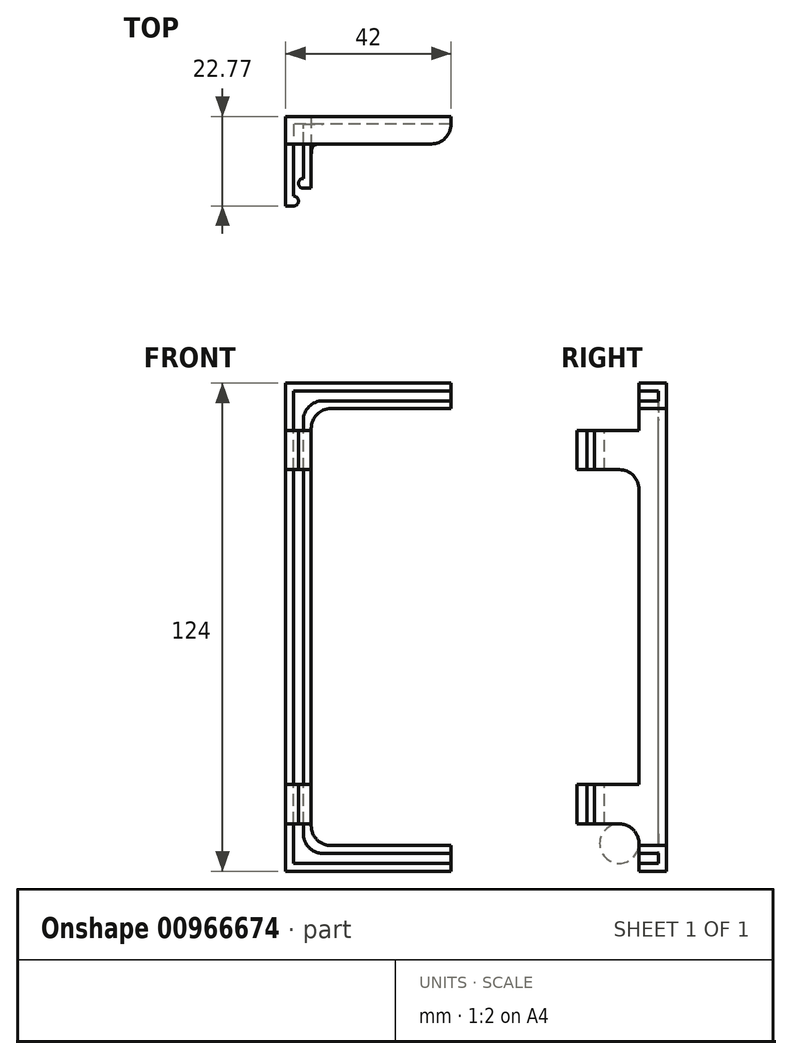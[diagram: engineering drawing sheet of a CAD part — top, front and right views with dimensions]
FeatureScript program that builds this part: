
annotation { "Feature Type Name" : "Feature", "Feature Type Description" : "" }
export const myFeature = defineFeature(function(context is Context, id is Id, definition is map)
    precondition{}
    {
        {
            var Q0;
            Q0=qCreatedBy(makeId("Top.planeOp"),FACE);
            var sketch = newSketch(context, id + "F0", { "sketchPlane" : qUnion([Q0])});
            skArc(sketch, "E0", {"start": v(0, -2.5) * mm, "mid": v(1.25, -1.25) * mm, "end": v(0, 0) * mm});
            skLineSegment(sketch, "E1", {"start": v(0, -1.25) * mm, "end": v(0, 11.7) * mm, "construction": true});
            skLineSegment(sketch, "E2", {"start": v(0, 2) * mm, "end": v(2.5, 2) * mm, "construction": true});
            skLineSegment(sketch, "E3", {"start": v(2.5, 2) * mm, "end": v(2.5, 8.7) * mm, "construction": true});
            skArc(sketch, "E4", {"start": v(2.5, 4.5) * mm, "mid": v(1.25, 3.25) * mm, "end": v(2.5, 2) * mm});
            skLineSegment(sketch, "E5", {"start": v(0, -2.5) * mm, "end": v(-2, -2.5) * mm});
            skLineSegment(sketch, "E6", {"start": v(-2, -2.5) * mm, "end": v(-2, 20.27) * mm});
            skLineSegment(sketch, "E7", {"start": v(2.5, 2) * mm, "end": v(4.5, 2) * mm});
            skLineSegment(sketch, "E8", {"start": v(4.5, 2) * mm, "end": v(4.5, 20.27) * mm});
            skLineSegment(sketch, "E9", {"start": v(4.5, 20.27) * mm, "end": v(-2, 20.27) * mm});
            skLineSegment(sketch, "E10", {"start": v(2.5, 4.5) * mm, "end": v(2.5, 18.27) * mm});
            skLineSegment(sketch, "E11", {"start": v(0, 0) * mm, "end": v(0, 18.27) * mm});
            skLineSegment(sketch, "E12", {"start": v(0, 18.27) * mm, "end": v(2.5, 18.27) * mm});
            skLineSegment(sketch, "E13", {"start": v(4.5, 13.27) * mm, "end": v(-2, 13.27) * mm});
            skSolve(sketch);
        }
        {
            var Q0;
            Q0=qCreatedBy(makeId("Front.planeOp"),FACE);
            var sketch = newSketch(context, id + "F1", { "sketchPlane" : qUnion([Q0])});
            skLineSegment(sketch, "E14", {"start": v(0, 0) * mm, "end": v(0, 120) * mm});
            skLineSegment(sketch, "E15", {"start": v(0, 120) * mm, "end": v(40, 120) * mm});
            skLineSegment(sketch, "E16", {"start": v(0, 0) * mm, "end": v(40, 0) * mm});
            skSolve(sketch);
        }
        {
            var Q0;
            {var subQ4=sQuery(id+"F0.wireOp",EDGE,"E9");Q0=makeQuery(id+"F0.imprint","IMPRINT",FACE,{"disambiguationData":[TD([[makeQuery(id+"F0.imprint","IMPRINT",EDGE,{"derivedFrom":subQ4}),1.0]])]});}
            var Q1;
            Q1=sQuery(id+"F1.wireOp",EDGE,"E14");
            var Q2;
            Q2=sQuery(id+"F1.wireOp",EDGE,"E15");
            var Q3;
            Q3=sQuery(id+"F1.wireOp",EDGE,"E16");
            sweep(context, id + "F2", {"profiles" : qUnion([Q0]), "path" : qUnion([Q1, Q2, Q3])});
        }
        {
            var Q0;
            Q0=qCreatedBy(makeId("Front.planeOp"),FACE);
            var sketch = newSketch(context, id + "F3", { "sketchPlane" : qUnion([Q0])});
            skLineSegment(sketch, "E17", {"start": v(0, 10) * mm, "end": v(0, 20) * mm});
            skLineSegment(sketch, "E18", {"start": v(0, 110) * mm, "end": v(0, 100) * mm});
            skSolve(sketch);
        }
        {
            var Q0;
            {var subQ1=sQuery(id+"F0.wireOp",EDGE,"E0");Q0=makeQuery(id+"F0.imprint","IMPRINT",FACE,{"disambiguationData":[TD([[makeQuery(id+"F0.imprint","IMPRINT",EDGE,{"derivedFrom":subQ1}),1.0]])]});}
            var Q1;
            Q1=sQuery(id+"F3.wireOp",VERTEX,"E17.start");
            cPlane(context, id + "F4", {"entities" : qUnion([Q0, Q1]), "cplaneType" : CPlaneType.PLANE_POINT, "offset" : 25 * mm, "width" : 150 * mm, "height" : 150 * mm});
        }
        {
            var Q0;
            {var subQ1=sQuery(id+"F0.wireOp",EDGE,"E0");Q0=makeQuery(id+"F0.imprint","IMPRINT",FACE,{"disambiguationData":[TD([[makeQuery(id+"F0.imprint","IMPRINT",EDGE,{"derivedFrom":subQ1}),1.0]])]});}
            var Q1;
            Q1=sQuery(id+"F3.wireOp",VERTEX,"E18.end");
            cPlane(context, id + "F5", {"entities" : qUnion([Q0, Q1]), "cplaneType" : CPlaneType.PLANE_POINT, "offset" : 25 * mm, "width" : 150 * mm, "height" : 150 * mm});
        }
        {
            var Q0;
            Q0=qCreatedBy(id+"F4.planeOp",FACE);
            var sketch = newSketch(context, id + "F6", { "sketchPlane" : qUnion([Q0])});
            skLineSegment(sketch, "E19.0.0", {"start": v(0, 0) * mm, "end": v(0, 13.27) * mm});
            skLineSegment(sketch, "E19.0.1", {"start": v(0, 13.27) * mm, "end": v(-2, 13.27) * mm});
            skLineSegment(sketch, "E19.0.2", {"start": v(-2, 13.27) * mm, "end": v(-2, -2.5) * mm});
            skLineSegment(sketch, "E19.0.3", {"start": v(-2, -2.5) * mm, "end": v(0, -2.5) * mm});
            skArc(sketch, "E19.0.4", {"start": v(0, -2.5) * mm, "mid": v(1.25, -1.25) * mm, "end": v(0, 0) * mm});
            skLineSegment(sketch, "E20.0.0", {"start": v(2.5, 13.27) * mm, "end": v(2.5, 4.5) * mm});
            skArc(sketch, "E20.0.1", {"start": v(2.5, 4.5) * mm, "mid": v(1.25, 3.25) * mm, "end": v(2.5, 2) * mm});
            skLineSegment(sketch, "E20.0.2", {"start": v(2.5, 2) * mm, "end": v(4.5, 2) * mm});
            skLineSegment(sketch, "E20.0.3", {"start": v(4.5, 2) * mm, "end": v(4.5, 13.27) * mm});
            skLineSegment(sketch, "E20.0.4", {"start": v(4.5, 13.27) * mm, "end": v(2.5, 13.27) * mm});
            skSolve(sketch);
        }
        {
            var Q0;
            Q0=qCreatedBy(id+"F5.planeOp",FACE);
            var sketch = newSketch(context, id + "F7", { "sketchPlane" : qUnion([Q0])});
            skLineSegment(sketch, "E21.0.0", {"start": v(0, 0) * mm, "end": v(0, 13.27) * mm});
            skLineSegment(sketch, "E21.0.1", {"start": v(0, 13.27) * mm, "end": v(-2, 13.27) * mm});
            skLineSegment(sketch, "E21.0.2", {"start": v(-2, 13.27) * mm, "end": v(-2, -2.5) * mm});
            skLineSegment(sketch, "E21.0.3", {"start": v(-2, -2.5) * mm, "end": v(0, -2.5) * mm});
            skArc(sketch, "E21.0.4", {"start": v(0, -2.5) * mm, "mid": v(1.25, -1.25) * mm, "end": v(0, 0) * mm});
            skLineSegment(sketch, "E22.0.0", {"start": v(2.5, 13.27) * mm, "end": v(2.5, 4.5) * mm});
            skArc(sketch, "E22.0.1", {"start": v(2.5, 4.5) * mm, "mid": v(1.25, 3.25) * mm, "end": v(2.5, 2) * mm});
            skLineSegment(sketch, "E22.0.2", {"start": v(2.5, 2) * mm, "end": v(4.5, 2) * mm});
            skLineSegment(sketch, "E22.0.3", {"start": v(4.5, 2) * mm, "end": v(4.5, 13.27) * mm});
            skLineSegment(sketch, "E22.0.4", {"start": v(4.5, 13.27) * mm, "end": v(2.5, 13.27) * mm});
            skSolve(sketch);
        }
        {
            var Q0;
            Q0=makeQuery(id+"F6.imprint","IMPRINT",FACE,{"disambiguationData":[TD([[makeQuery(id+"F6.imprint","IMPRINT",EDGE,{"derivedFrom":sQuery(id+"F6.wireOp",EDGE,"E19.0.0")}),1.0]])]});
            var Q1;
            Q1=makeQuery(id+"F6.imprint","IMPRINT",FACE,{"disambiguationData":[TD([[makeQuery(id+"F6.imprint","IMPRINT",EDGE,{"derivedFrom":sQuery(id+"F6.wireOp",EDGE,"E20.0.0")}),1.0]])]});
            var Q2;
            Q2=sQuery(id+"F3.wireOp",EDGE,"E17");
            sweep(context, id + "F8", {"operationType" : NewBodyOperationType.ADD, "profiles" : qUnion([Q0, Q1]), "path" : qUnion([Q2])});
        }
        {
            var Q0;
            Q0=makeQuery(id+"F7.imprint","IMPRINT",FACE,{"disambiguationData":[TD([[makeQuery(id+"F7.imprint","IMPRINT",EDGE,{"derivedFrom":sQuery(id+"F7.wireOp",EDGE,"E21.0.0")}),1.0]])]});
            var Q1;
            Q1=makeQuery(id+"F7.imprint","IMPRINT",FACE,{"disambiguationData":[TD([[makeQuery(id+"F7.imprint","IMPRINT",EDGE,{"derivedFrom":sQuery(id+"F7.wireOp",EDGE,"E22.0.0")}),1.0]])]});
            var Q2;
            Q2=sQuery(id+"F3.wireOp",EDGE,"E18");
            sweep(context, id + "F9", {"operationType" : NewBodyOperationType.ADD, "profiles" : qUnion([Q0, Q1]), "path" : qUnion([Q2])});
        }
        {
            var Q0;
            Q0=makeQuery(id+"F8.opSweep","CAP_EDGE",EDGE,{"disambiguationData":[OSD([sQuery(id+"F3.wireOp",VERTEX,"E17.start"),sQuery(id+"F6.wireOp",EDGE,"E19.0.1")])],"isStart":true});
            var Q1;
            Q1=makeQuery(id+"F8.opSweep","CAP_EDGE",EDGE,{"disambiguationData":[OSD([sQuery(id+"F3.wireOp",VERTEX,"E17.start"),sQuery(id+"F6.wireOp",EDGE,"E20.0.4")])],"isStart":true});
            var Q2;
            Q2=makeQuery(id+"F8.opSweep","CAP_EDGE",EDGE,{"disambiguationData":[OSD([sQuery(id+"F3.wireOp",VERTEX,"E17.end"),sQuery(id+"F6.wireOp",EDGE,"E19.0.1")])],"isStart":false});
            var Q3;
            Q3=makeQuery(id+"F8.opSweep","CAP_EDGE",EDGE,{"disambiguationData":[OSD([sQuery(id+"F3.wireOp",VERTEX,"E17.end"),sQuery(id+"F6.wireOp",EDGE,"E20.0.4")])],"isStart":false});
            var Q4;
            Q4=makeQuery(id+"F9.opSweep","CAP_EDGE",EDGE,{"disambiguationData":[OSD([sQuery(id+"F3.wireOp",VERTEX,"E18.end"),sQuery(id+"F7.wireOp",EDGE,"E21.0.1")])],"isStart":true});
            var Q5;
            Q5=makeQuery(id+"F9.opSweep","CAP_EDGE",EDGE,{"disambiguationData":[OSD([sQuery(id+"F3.wireOp",VERTEX,"E18.end"),sQuery(id+"F7.wireOp",EDGE,"E22.0.4")])],"isStart":true});
            var Q6;
            Q6=makeQuery(id+"F9.opSweep","CAP_EDGE",EDGE,{"disambiguationData":[OSD([sQuery(id+"F3.wireOp",VERTEX,"E18.start"),sQuery(id+"F7.wireOp",EDGE,"E22.0.4")])],"isStart":false});
            var Q7;
            Q7=makeQuery(id+"F9.opSweep","CAP_EDGE",EDGE,{"disambiguationData":[OSD([sQuery(id+"F3.wireOp",VERTEX,"E18.start"),sQuery(id+"F7.wireOp",EDGE,"E21.0.1")])],"isStart":false});
            fillet(context, id + "F10", {"entities" : qUnion([Q0, Q1, Q2, Q3, Q4, Q5, Q6, Q7]), "radius" : 5 * mm, "tangentPropagation" : true, "allowEdgeOverflow" : false});
        }
        {
            var Q0;
            Q0=makeQuery(id+"F2.opSweep","MID_CAP_EDGE",EDGE,{"disambiguationData":[OSD([sQuery(id+"F0.wireOp",EDGE,"E10"),sQuery(id+"F1.wireOp",VERTEX,"E15.start")])],"capPos":2.0});
            var Q1;
            Q1=makeQuery(id+"F2.opSweep","MID_CAP_EDGE",EDGE,{"disambiguationData":[OSD([sQuery(id+"F0.wireOp",EDGE,"E8"),sQuery(id+"F1.wireOp",VERTEX,"E15.start")])],"capPos":2.0});
            var Q2;
            Q2=makeQuery(id+"F2.opSweep","MID_CAP_EDGE",EDGE,{"disambiguationData":[OSD([sQuery(id+"F0.wireOp",EDGE,"E8"),sQuery(id+"F1.wireOp",VERTEX,"E16.start")])],"capPos":1.0});
            var Q3;
            Q3=makeQuery(id+"F2.opSweep","MID_CAP_EDGE",EDGE,{"disambiguationData":[OSD([sQuery(id+"F0.wireOp",EDGE,"E10"),sQuery(id+"F1.wireOp",VERTEX,"E16.start")])],"capPos":1.0});
            fillet(context, id + "F11", {"entities" : qUnion([Q0, Q1, Q2, Q3]), "radius" : 5 * mm, "tangentPropagation" : true, "allowEdgeOverflow" : false});
        }
        {
            var Q0;
            {var subQ0=sQuery(id+"F1.wireOp",VERTEX,"E16.end");var subQ1=sQuery(id+"F0.wireOp",EDGE,"E13");Q0=makeQuery(id+"F2.opSweep","CAP_EDGE",EDGE,{"disambiguationData":[OSD([subQ1,subQ0]),TDD([makeQuery(id+"F0.imprint","IMPRINT",EDGE,{"disambiguationData":[TD([[makeQuery(id+"F0.imprint","INTERSECT",VERTEX,{"derivedFrom":[sQuery(id+"F0.wireOp",EDGE,"E6"),subQ1]}),1.0]])],"derivedFrom":subQ1}),subQ0])],"isStart":true});}
            var Q1;
            {var subQ0=sQuery(id+"F1.wireOp",VERTEX,"E16.end");var subQ1=sQuery(id+"F0.wireOp",EDGE,"E13");Q1=makeQuery(id+"F2.opSweep","CAP_EDGE",EDGE,{"disambiguationData":[OSD([subQ1,subQ0]),TDD([makeQuery(id+"F0.imprint","IMPRINT",EDGE,{"disambiguationData":[TD([[makeQuery(id+"F0.imprint","INTERSECT",VERTEX,{"derivedFrom":[sQuery(id+"F0.wireOp",EDGE,"E8"),subQ1]}),-1.0]])],"derivedFrom":subQ1}),subQ0])],"isStart":true});}
            var Q2;
            {var subQ0=sQuery(id+"F1.wireOp",VERTEX,"E15.end");var subQ1=sQuery(id+"F0.wireOp",EDGE,"E13");Q2=makeQuery(id+"F2.opSweep","CAP_EDGE",EDGE,{"disambiguationData":[OSD([subQ1,subQ0]),TDD([makeQuery(id+"F0.imprint","IMPRINT",EDGE,{"disambiguationData":[TD([[makeQuery(id+"F0.imprint","INTERSECT",VERTEX,{"derivedFrom":[sQuery(id+"F0.wireOp",EDGE,"E8"),subQ1]}),-1.0]])],"derivedFrom":subQ1}),subQ0])],"isStart":false});}
            var Q3;
            {var subQ0=sQuery(id+"F1.wireOp",VERTEX,"E15.end");var subQ1=sQuery(id+"F0.wireOp",EDGE,"E13");Q3=makeQuery(id+"F2.opSweep","CAP_EDGE",EDGE,{"disambiguationData":[OSD([subQ1,subQ0]),TDD([makeQuery(id+"F0.imprint","IMPRINT",EDGE,{"disambiguationData":[TD([[makeQuery(id+"F0.imprint","INTERSECT",VERTEX,{"derivedFrom":[sQuery(id+"F0.wireOp",EDGE,"E6"),subQ1]}),1.0]])],"derivedFrom":subQ1}),subQ0])],"isStart":false});}
            fillet(context, id + "F12", {"entities" : qUnion([Q0, Q1, Q2, Q3]), "radius" : 5 * mm, "tangentPropagation" : true, "allowEdgeOverflow" : false});
        }
    });
